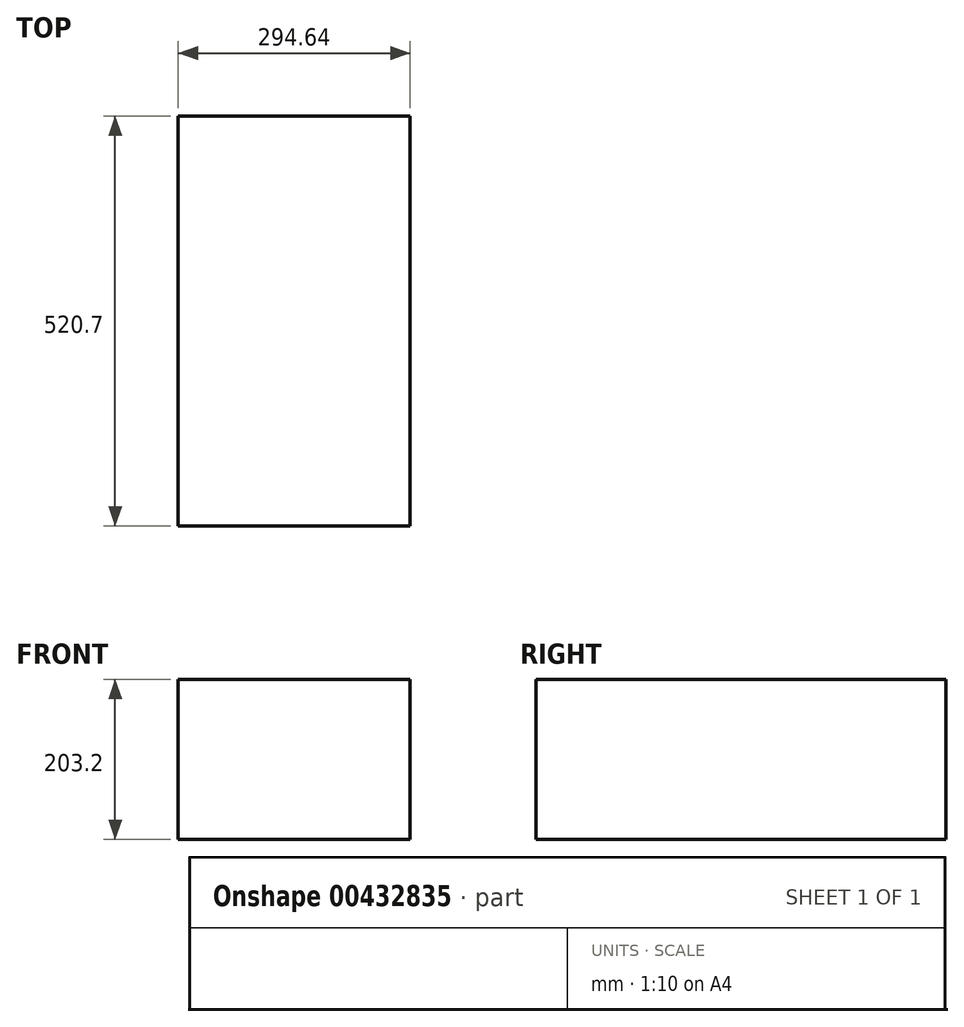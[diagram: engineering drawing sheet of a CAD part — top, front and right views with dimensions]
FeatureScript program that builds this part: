
annotation { "Feature Type Name" : "Feature", "Feature Type Description" : "" }
export const myFeature = defineFeature(function(context is Context, id is Id, definition is map)
    precondition{}
    {
        {
            var Q0;
            Q0=qCreatedBy(makeId("Front.planeOp"),FACE);
            var sketch = newSketch(context, id + "F0", { "sketchPlane" : qUnion([Q0])});
            skLineSegment(sketch, "E0.bottom", {"start": v(147.32, 101.6) * mm, "end": v(-147.32, 101.6) * mm});
            skLineSegment(sketch, "E0.top", {"start": v(147.32, -101.6) * mm, "end": v(-147.32, -101.6) * mm});
            skLineSegment(sketch, "E0.left", {"start": v(147.32, 101.6) * mm, "end": v(147.32, -101.6) * mm});
            skLineSegment(sketch, "E0.right", {"start": v(-147.32, 101.6) * mm, "end": v(-147.32, -101.6) * mm});
            skPoint(sketch, "E0.middle", {"position": v(0, 0) * mm});
            skSolve(sketch);
        }
        {
            var Q0;
            Q0 = qSketchRegion(id + "F0", true);
            extrude(context, id + "F1", {"entities" : qUnion([Q0]), "depth" : 520.7 * mm});
        }
        {
            var Q0;
            Q0 = qSketchRegion(id + "F0", true);
            extrude(context, id + "F2", {"entities" : qUnion([Q0]), "operationType" : NewBodyOperationType.ADD, "depth" : 69.85 * mm});
        }
    });
